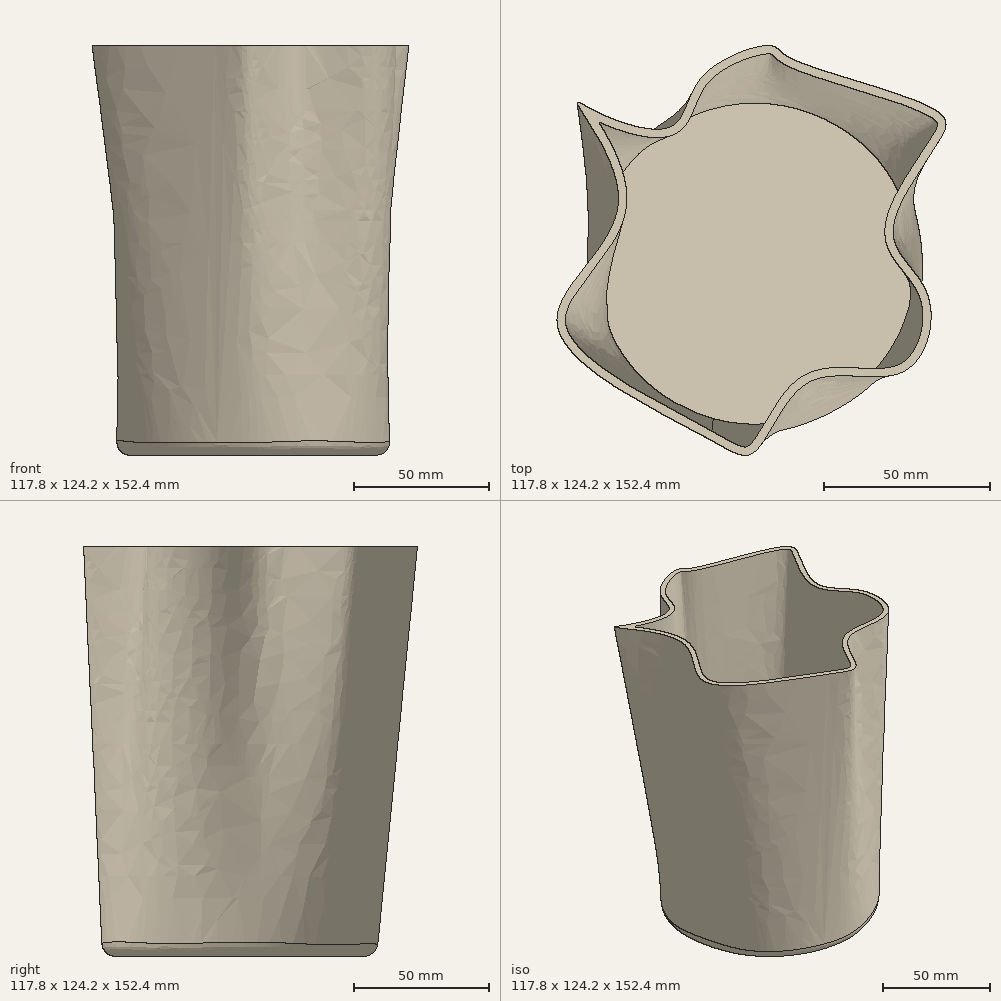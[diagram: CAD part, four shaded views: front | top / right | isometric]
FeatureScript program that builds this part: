
annotation { "Feature Type Name" : "Feature", "Feature Type Description" : "" }
export const myFeature = defineFeature(function(context is Context, id is Id, definition is map)
    precondition{}
    {
        {
            var Q0;
            Q0=qCreatedBy(makeId("Top.planeOp"),FACE);
            var sketch = newSketch(context, id + "F0", { "sketchPlane" : qUnion([Q0])});
            skCircle(sketch, "E0", {"center": v(0, 0) * mm, "radius": 51 * mm});
            skSolve(sketch);
        }
        {
            var Q0;
            Q0=qCreatedBy(makeId("Top.planeOp"),FACE);
            cPlane(context, id + "F1", {"entities" : qUnion([Q0]), "cplaneType" : CPlaneType.OFFSET, "offset" : 152.4 * mm, "width" : 152.4 * mm, "height" : 152.4 * mm});
        }
        {
            var Q0;
            Q0=qCreatedBy(id+"F1.planeOp",FACE);
            var sketch = newSketch(context, id + "F2", { "sketchPlane" : qUnion([Q0])});
            skFitSpline(sketch, "E1", {"points": [v(-14.28, -52.87) * mm, v(0, -56.94) * mm, v(16.57, -35.79) * mm, v(45.36, -32.5) * mm, v(52.27, -9.27) * mm, v(41.87, 9) * mm, v(55.71, 36.9) * mm, v(55.74, 45.83) * mm, v(10.05, 62.7) * mm, v(4.91, 66.1) * mm, v(-16.1, 56.45) * mm, v(-25.23, 41.62) * mm, v(-48.77, 46.5) * mm, v(-53.9, 48.8) * mm, v(-41.38, 18.36) * mm, v(-59.9, -18.14) * mm, v(-14.28, -52.87) * mm]});
            skSolve(sketch);
        }
        {
            var Q0;
            Q0=makeQuery(id+"F2.imprint","IMPRINT",FACE,{"disambiguationData":[TD([[makeQuery(id+"F2.imprint","IMPRINT",EDGE,{"derivedFrom":sQuery(id+"F2.wireOp",EDGE,"E1")}),1.0]])]});
            var Q1;
            Q1=makeQuery(id+"F0.imprint","IMPRINT",FACE,{"disambiguationData":[TD([[makeQuery(id+"F0.imprint","IMPRINT",EDGE,{"derivedFrom":sQuery(id+"F0.wireOp",EDGE,"E0")}),1.0]])]});
            loft(context, id + "F3", {"sheetProfilesArray" : [{ "sheetProfileEntities" : qUnion([Q0]) }, { "sheetProfileEntities" : qUnion([Q1]) }]});
        }
        {
            var Q0;
            Q0=makeQuery(id+"F3.opLoft","CAP_FACE",FACE,{"disambiguationData":[OSD([makeQuery(id+"F2.imprint","IMPRINT",FACE,{"disambiguationData":[TD([[makeQuery(id+"F2.imprint","IMPRINT",EDGE,{"derivedFrom":sQuery(id+"F2.wireOp",EDGE,"E1")}),1.0]])]})])],"isStart":true});
            shell(context, id + "F4", {"entities" : qUnion([Q0]), "thickness" : 2.54 * mm});
        }
        {
            var Q0;
            Q0=makeQuery(id+"F3.opLoft","MID_CAP_EDGE",EDGE,{"disambiguationData":[OSD([sQuery(id+"F0.wireOp",EDGE,"E0"),sQuery(id+"F2.wireOp",EDGE,"E1")])],"capPos":1.0});
            fillet(context, id + "F5", {"entities" : qUnion([Q0]), "radius" : 5.08 * mm, "tangentPropagation" : true, "allowEdgeOverflow" : false});
        }
    });
